# Revit family: EZTS(24x16)+ NO HWC
name_source: partatom
category: Mechanical Equipment
revit_build: Autodesk Revit 2018 (Build: 20170223_1515(x64)
units: mm (PartAtom-declared; Revit-internal decimal feet)

## family parameters
Always vertical = Yes
Cut with Voids When Loaded = No
Part Type = Normal
Room Calculation Point = No
Round Connector Dimension = Use Radius
Shared = No
Work Plane-Based = No

## types (3) — shared parameters
Controller Center = 5 11/16"
Controller Depth = 7 1/8"
Controller Length = 14 7/32"
Controller Offset = 3"
Duct Discharge Height = 18"
Duct Discharge Width = 38"
Duct Inlet Dia = 16"
Height = 18"
Inlet Center = 9"
Inlet Depth = 5 7/16"
Length = 30"
Manufacturer = Anemostat Products
Model = EZTS+
URL = https://www.anemostat-hvac.com
Width = 38"

## per-type parameters (varying)
| type | Controller Left | Controller Right | Description |
| EZTS(24x16)+ with NO Controller | No | No | SINGLE DUCT AIR TERMINAL WITH INTEGRAL |
| EZTS(24x16)+ With Controller RH | No | Yes | SINGLE DUCT AIR TERMINAL WITH INTEGRAL ATTENUATOR |
| EZTS(24x16)+ With Controller LH | Yes | No | SINGLE DUCT AIR TERMINAL WITH INTEGRAL |

## geometry (parser evidence)
native form markers: Sweep x2
no freeform markers — native parametric forms only
